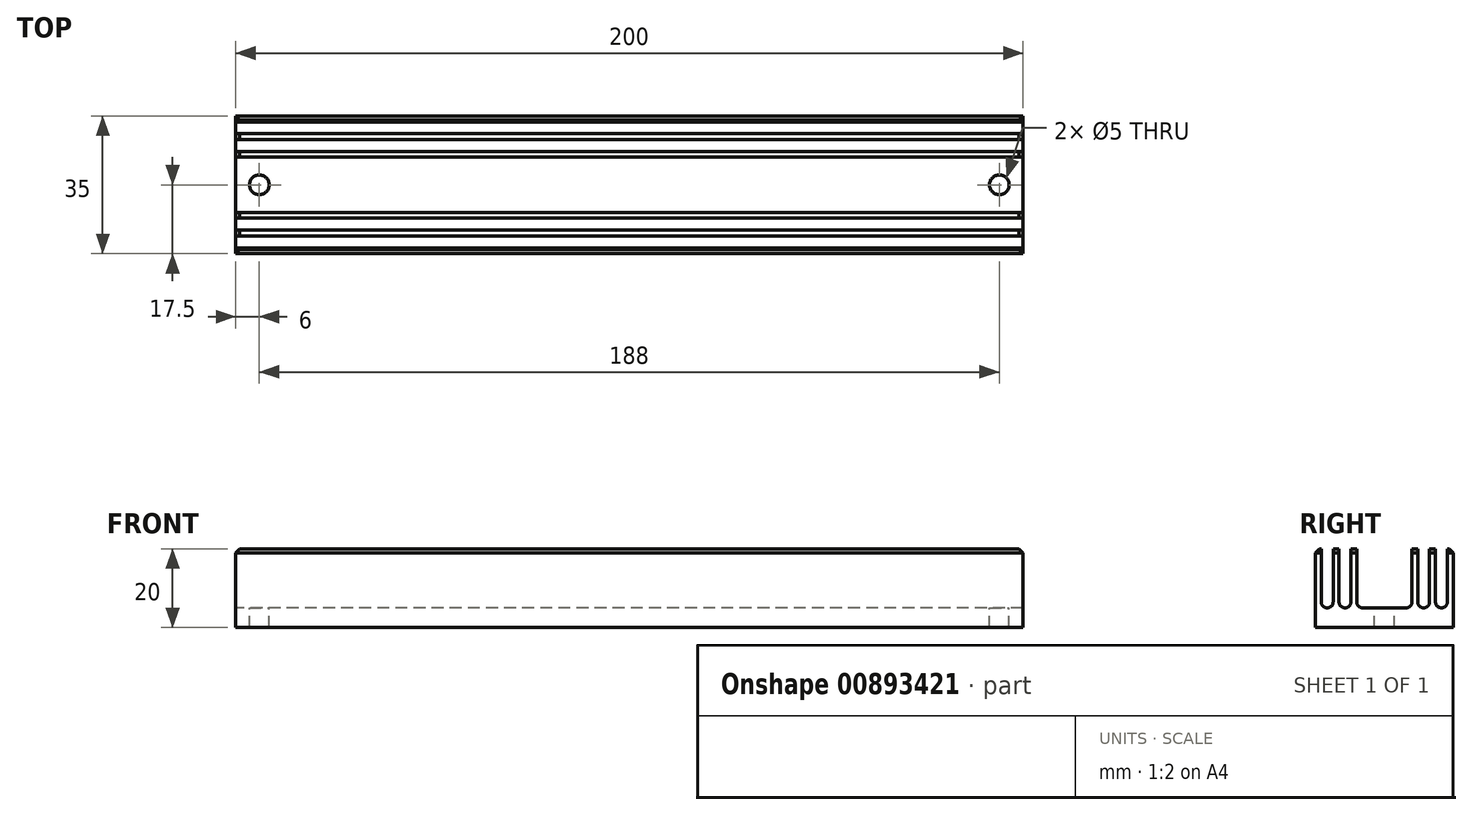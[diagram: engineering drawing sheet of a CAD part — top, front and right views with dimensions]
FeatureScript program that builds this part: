
annotation { "Feature Type Name" : "Feature", "Feature Type Description" : "" }
export const myFeature = defineFeature(function(context is Context, id is Id, definition is map)
    precondition{}
    {
        {
            var Q0;
            Q0=qCreatedBy(makeId("Top.planeOp"),FACE);
            var sketch = newSketch(context, id + "F0", { "sketchPlane" : qUnion([Q0])});
            skLineSegment(sketch, "E0.bottom", {"start": v(-100, 17.5) * mm, "end": v(100, 17.5) * mm});
            skLineSegment(sketch, "E0.top", {"start": v(-100, -17.5) * mm, "end": v(100, -17.5) * mm});
            skLineSegment(sketch, "E0.left", {"start": v(-100, 17.5) * mm, "end": v(-100, -17.5) * mm});
            skLineSegment(sketch, "E0.right", {"start": v(100, 17.5) * mm, "end": v(100, -17.5) * mm});
            skSolve(sketch);
        }
        {
            var Q0;
            Q0=makeQuery(id+"F0.imprint","IMPRINT",FACE,{"disambiguationData":[TD([[makeQuery(id+"F0.imprint","IMPRINT",EDGE,{"derivedFrom":sQuery(id+"F0.wireOp",EDGE,"E0.bottom")}),-1.0]])]});
            extrude(context, id + "F1", {"entities" : qUnion([Q0]), "depth" : 20 * mm, "offsetDistance" : 25 * mm});
        }
        {
            var Q0;
            Q0=makeQuery(id+"F1.opExtrude","CAP_FACE",FACE,{"disambiguationData":[OSD([sQuery(id+"F0.wireOp",EDGE,"E0.bottom"),sQuery(id+"F0.wireOp",EDGE,"E0.top"),sQuery(id+"F0.wireOp",EDGE,"E0.left"),sQuery(id+"F0.wireOp",EDGE,"E0.right")])],"isStart":false});
            var sketch = newSketch(context, id + "F2", { "sketchPlane" : qUnion([Q0])});
            skCircle(sketch, "E1", {"center": v(-94, 0) * mm, "radius": 2.5 * mm});
            skPoint(sketch, "E1.centerSnap0", {"position": v(-100, 0) * mm});
            skCircle(sketch, "E2", {"center": v(94, 0) * mm, "radius": 2.5 * mm});
            skPoint(sketch, "E2.centerSnap0", {"position": v(100, 0) * mm});
            skSolve(sketch);
        }
        {
            var Q0;
            Q0=makeQuery(id+"F2.imprint","IMPRINT",FACE,{"disambiguationData":[TD([[makeQuery(id+"F2.imprint","IMPRINT",EDGE,{"derivedFrom":sQuery(id+"F2.wireOp",EDGE,"E1")}),1.0]])]});
            var Q1;
            Q1=makeQuery(id+"F2.imprint","IMPRINT",FACE,{"disambiguationData":[TD([[makeQuery(id+"F2.imprint","IMPRINT",EDGE,{"derivedFrom":sQuery(id+"F2.wireOp",EDGE,"E2")}),1.0]])]});
            extrude(context, id + "F3", {"entities" : qUnion([Q0, Q1]), "operationType" : NewBodyOperationType.REMOVE, "oppositeDirection" : true, "depth" : 25 * mm, "offsetDistance" : 25 * mm});
        }
        {
            var Q0;
            Q0=makeQuery(id+"F1.opExtrude","CAP_FACE",FACE,{"disambiguationData":[OSD([sQuery(id+"F0.wireOp",EDGE,"E0.bottom"),sQuery(id+"F0.wireOp",EDGE,"E0.top"),sQuery(id+"F0.wireOp",EDGE,"E0.left"),sQuery(id+"F0.wireOp",EDGE,"E0.right")])],"isStart":false});
            chamfer(context, id + "F4", {"entities" : qUnion([Q0]), "width" : (1) * mm, "tangentPropagation" : true});
        }
        {
            var Q0;
            Q0=makeQuery(id+"F1.opExtrude","SWEPT_FACE",FACE,{"disambiguationData":[OSD([sQuery(id+"F0.wireOp",EDGE,"E0.left")])]});
            var sketch = newSketch(context, id + "F5", { "sketchPlane" : qUnion([Q0])});
            skLineSegment(sketch, "E3.bottom", {"start": v(-16, 21.05) * mm, "end": v(-13, 21.05) * mm});
            skLineSegment(sketch, "E3.top", {"start": v(-14.5, 5) * mm, "end": v(-14.5, 5) * mm});
            skLineSegment(sketch, "E3.left", {"start": v(-16, 21.05) * mm, "end": v(-16, 6.5) * mm});
            skLineSegment(sketch, "E3.right", {"start": v(-13, 21.05) * mm, "end": v(-13, 6.5) * mm});
            skLineSegment(sketch, "E4.bottom", {"start": v(-11.5, 21.05) * mm, "end": v(-8.5, 21.05) * mm});
            skLineSegment(sketch, "E4.top", {"start": v(-10, 5) * mm, "end": v(-10, 5) * mm});
            skLineSegment(sketch, "E4.left", {"start": v(-11.5, 21.05) * mm, "end": v(-11.5, 6.5) * mm});
            skLineSegment(sketch, "E4.right", {"start": v(-8.5, 21.05) * mm, "end": v(-8.5, 6.5) * mm});
            skLineSegment(sketch, "E5.bottom", {"start": v(-7, 20.95) * mm, "end": v(-4, 20.95) * mm});
            skLineSegment(sketch, "E5.top", {"start": v(-5.5, 5) * mm, "end": v(-5.5, 5) * mm});
            skLineSegment(sketch, "E5.left", {"start": v(-7, 20.95) * mm, "end": v(-7, 6.5) * mm});
            skLineSegment(sketch, "E5.right", {"start": v(-4, 20.95) * mm, "end": v(-4, 6.5) * mm});
            skLineSegment(sketch, "E6.bottom", {"start": v(8.5, 21) * mm, "end": v(11.5, 21) * mm});
            skLineSegment(sketch, "E6.top", {"start": v(10, 5) * mm, "end": v(10, 5) * mm});
            skLineSegment(sketch, "E6.left", {"start": v(8.5, 21) * mm, "end": v(8.5, 6.5) * mm});
            skLineSegment(sketch, "E6.right", {"start": v(11.5, 21) * mm, "end": v(11.5, 6.5) * mm});
            skLineSegment(sketch, "E7.bottom", {"start": v(13, 21) * mm, "end": v(16, 21) * mm});
            skLineSegment(sketch, "E7.top", {"start": v(14.5, 5) * mm, "end": v(14.5, 5) * mm});
            skLineSegment(sketch, "E7.left", {"start": v(13, 21) * mm, "end": v(13, 6.5) * mm});
            skLineSegment(sketch, "E7.right", {"start": v(16, 21) * mm, "end": v(16, 6.5) * mm});
            skLineSegment(sketch, "E8.bottom", {"start": v(4, 21) * mm, "end": v(7, 21) * mm});
            skLineSegment(sketch, "E8.top", {"start": v(5.5, 5) * mm, "end": v(5.5, 5) * mm});
            skLineSegment(sketch, "E8.left", {"start": v(4, 21) * mm, "end": v(4, 6.5) * mm});
            skLineSegment(sketch, "E8.right", {"start": v(7, 21) * mm, "end": v(7, 6.5) * mm});
            skPoint(sketch, "E9.visualSharp", {"position": v(-16, 5) * mm});
            skArc(sketch, "E9.filletArc", {"start": v(-16, 6.5) * mm, "mid": v(-15.56, 5.44) * mm, "end": v(-14.5, 5) * mm});
            skPoint(sketch, "E10.visualSharp", {"position": v(-13, 5) * mm});
            skArc(sketch, "E10.filletArc", {"start": v(-14.5, 5) * mm, "mid": v(-13.44, 5.44) * mm, "end": v(-13, 6.5) * mm});
            skPoint(sketch, "E11.visualSharp", {"position": v(-11.5, 5) * mm});
            skArc(sketch, "E11.filletArc", {"start": v(-11.5, 6.5) * mm, "mid": v(-11.06, 5.44) * mm, "end": v(-10, 5) * mm});
            skPoint(sketch, "E12.visualSharp", {"position": v(-8.5, 5) * mm});
            skArc(sketch, "E12.filletArc", {"start": v(-10, 5) * mm, "mid": v(-8.94, 5.44) * mm, "end": v(-8.5, 6.5) * mm});
            skPoint(sketch, "E13.visualSharp", {"position": v(-7, 5) * mm});
            skArc(sketch, "E13.filletArc", {"start": v(-7, 6.5) * mm, "mid": v(-6.56, 5.44) * mm, "end": v(-5.5, 5) * mm});
            skPoint(sketch, "E14.visualSharp", {"position": v(-4, 5) * mm});
            skArc(sketch, "E14.filletArc", {"start": v(-5.5, 5) * mm, "mid": v(-4.44, 5.44) * mm, "end": v(-4, 6.5) * mm});
            skPoint(sketch, "E15.visualSharp", {"position": v(4, 5) * mm});
            skArc(sketch, "E15.filletArc", {"start": v(4, 6.5) * mm, "mid": v(4.44, 5.44) * mm, "end": v(5.5, 5) * mm});
            skPoint(sketch, "E16.visualSharp", {"position": v(7, 5) * mm});
            skArc(sketch, "E16.filletArc", {"start": v(5.5, 5) * mm, "mid": v(6.56, 5.44) * mm, "end": v(7, 6.5) * mm});
            skPoint(sketch, "E17.visualSharp", {"position": v(8.5, 5) * mm});
            skArc(sketch, "E17.filletArc", {"start": v(8.5, 6.5) * mm, "mid": v(8.94, 5.44) * mm, "end": v(10, 5) * mm});
            skPoint(sketch, "E18.visualSharp", {"position": v(11.5, 5) * mm});
            skArc(sketch, "E18.filletArc", {"start": v(10, 5) * mm, "mid": v(11.06, 5.44) * mm, "end": v(11.5, 6.5) * mm});
            skPoint(sketch, "E19.visualSharp", {"position": v(13, 5) * mm});
            skArc(sketch, "E19.filletArc", {"start": v(13, 6.5) * mm, "mid": v(13.44, 5.44) * mm, "end": v(14.5, 5) * mm});
            skPoint(sketch, "E20.visualSharp", {"position": v(16, 5) * mm});
            skArc(sketch, "E20.filletArc", {"start": v(14.5, 5) * mm, "mid": v(15.56, 5.44) * mm, "end": v(16, 6.5) * mm});
            skSolve(sketch);
        }
        {
            var Q0;
            Q0 = qSketchRegion(id + "F5", true);
            extrude(context, id + "F6", {"entities" : qUnion([Q0]), "operationType" : NewBodyOperationType.REMOVE, "oppositeDirection" : true, "depth" : 240 * mm, "offsetDistance" : 25 * mm});
        }
        {
            var Q0;
            Q0=makeQuery(id+"F1.opExtrude","SWEPT_FACE",FACE,{"disambiguationData":[OSD([sQuery(id+"F0.wireOp",EDGE,"E0.left")])]});
            var sketch = newSketch(context, id + "F7", { "sketchPlane" : qUnion([Q0])});
            skLineSegment(sketch, "E21.bottom", {"start": v(-5.5, 21.4) * mm, "end": v(5.5, 21.4) * mm});
            skLineSegment(sketch, "E21.top", {"start": v(-5.5, 5) * mm, "end": v(5.5, 5) * mm});
            skLineSegment(sketch, "E21.left", {"start": v(-5.5, 21.4) * mm, "end": v(-5.5, 5) * mm});
            skLineSegment(sketch, "E21.right", {"start": v(5.5, 21.4) * mm, "end": v(5.5, 5) * mm});
            skSolve(sketch);
        }
        {
            var Q0;
            {var subQ6=sQuery(id+"F7.wireOp",EDGE,"E21.top");Q0=makeQuery(id+"F7.imprint","IMPRINT",FACE,{"disambiguationData":[TD([[makeQuery(id+"F7.imprint","IMPRINT",EDGE,{"derivedFrom":subQ6}),1.0]])]});}
            var Q1;
            Q1=makeQuery(id+"F7.imprint","IMPRINT",FACE,{"disambiguationData":[TD([[makeQuery(id+"F7.imprint","IMPRINT",EDGE,{"derivedFrom":sQuery(id+"F7.wireOp",EDGE,"E21.bottom")}),-1.0]])]});
            extrude(context, id + "F8", {"entities" : qUnion([Q0, Q1]), "operationType" : NewBodyOperationType.REMOVE, "oppositeDirection" : true, "depth" : 250 * mm, "offsetDistance" : 25 * mm});
        }
    });
